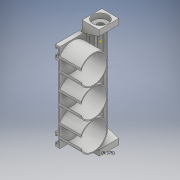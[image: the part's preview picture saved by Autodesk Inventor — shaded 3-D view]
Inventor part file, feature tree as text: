
AUTODESK INVENTOR PART (.ipt)
format: ipt  version: 2018 (Build 220112000, 112)  size: 696,320 bytes
history: native  units: mm
features: sketch x28, extrude x18, fillet x3, chamfer x2
ambient origin geometry x8: Origin, YZ Plane, XZ Plane, XY Plane, X Axis, Y Axis, Z Axis, Center Point
bodies: Solid1 (feature_tree)
feature tree (51):
  extrude  "Extrusion1"  Depth=125.0mm
  extrude  "Extrusion2"  Depth=15.0mm
  extrude  "Extrusion3"  Depth=22.0mm TaperAngle=0.0deg
  extrude  "Extrusion4"  Depth=22.0mm TaperAngle=0.0deg
  extrude  "Extrusion5"  Depth=155.0mm TaperAngle=0.0deg
  chamfer  "Chamfer1"  Distance=7.1mm
  sketch  "Sketch6"  dims[d16=22.0mm d17=7.1mm d18=0.0mm d19=7.0mm d20=2.0mm d21=12.61873mm]
  chamfer  "Chamfer2"  Distance=7.0mm
  sketch  "Sketch7"  dims[d22=7.0mm d23=2.0mm d24=12.61873mm d25=8.0mm]
  sketch  "Sketch8"  dims[d26=2.0mm d27=0.0mm d28=8.0mm]
  sketch  "Sketch9"  dims[d29=2.0mm d30=0.0mm d31=2.0mm d32=0.0mm]
  extrude  "Extrusion6"  Depth=8.0mm
  extrude  "Extrusion7"  Depth=8.0mm
  extrude  "Extrusion8"  Depth=2.0mm TaperAngle=0.0deg
  extrude  "Extrusion9"  Depth=2.0mm
  sketch  "Sketch13"  dims[d45=2.0mm d46=38.0mm]
  sketch  "Sketch14"  dims[d47=2.0mm d48=0.0mm d49=38.0mm]
  extrude  "Extrusion10"  Depth=2.0mm
  sketch  "Sketch16"  dims[d53=38.0mm d54=40.75mm]
  extrude  "Extrusion11"  Depth=7.0mm TaperAngle=0.0deg
  fillet  "Fillet1"  Radius=2.0mm
  fillet  "Fillet2"  Radius=2.0mm
  extrude  "Extrusion12"  Depth=2.0mm
  extrude  "Extrusion13"  Depth=2.0mm
  extrude  "Extrusion14"  Depth=21.75mm
  sketch  "Sketch21"  dims[d66=3.0mm]
  extrude  "Extrusion15"  Depth=40.75mm
  extrude  "Extrusion16"  Depth=40.75mm
  sketch  "Sketch24"  dims[d69=3.1mm d70=0.0mm]
  sketch  "Sketch25"  dims[d71=2.0mm]
  extrude  "Extrusion17"  Depth=32.0mm TaperAngle=0.0deg
  extrude  "Extrusion18"  Depth=3.0mm
  sketch  "Sketch28"  dims[d75=5.0mm d76=5.0mm d77=5.0mm d78=5.0mm d79=1.0mm d80=0.0mm d81=9.375mm d82=2.0mm]
  fillet  "Fillet3"  Radius=3.0mm
  sketch  "Sketch1"  dims[d0=24.0mm d1=125.0mm]
  sketch  "Sketch2"  dims[d2=2.0mm d3=0.0mm d4=15.0mm]
  sketch  "Sketch3"  dims[d5=15.0mm d6=22.0mm d7=2.0mm d8=0.0mm d9=0.0mm]
  sketch  "Sketch4"  dims[d10=22.0mm d11=7.1mm d12=0.0mm]
  sketch  "Sketch5"  dims[d13=9.0mm d14=155.0mm d15=0.0mm]
  sketch  "Sketch10"  dims[d33=2.0mm d34=0.0mm d35=5.5mm]
  sketch  "Sketch11"  dims[d36=11.0mm d37=2.0mm]
  sketch  "Sketch12"  dims[d38=2.0mm d39=7.0mm d40=0.0mm d42=2.0mm d43=0.0mm d44=2.0mm]
  sketch  "Sketch15"  dims[d51=43.5mm d52=21.75mm]
  sketch  "Sketch17"  dims[d55=38.0mm d56=40.75mm]
  sketch  "Sketch18"  dims[d57=30.0mm d58=0.0mm d59=32.0mm d60=0.0mm]
  sketch  "Sketch19"  dims[d61=3.0mm d62=12.0mm d63=3.0mm]
  sketch  "Sketch20"  dims[d64=3.1mm d65=0.0mm]
  sketch  "Sketch22"  dims[d67=12.0mm]
  sketch  "Sketch23"  dims[d68=3.0mm]
  sketch  "Sketch26"  dims[d72=2.0mm]
  sketch  "Sketch27"  dims[d73=3.6mm d74=0.0mm]
